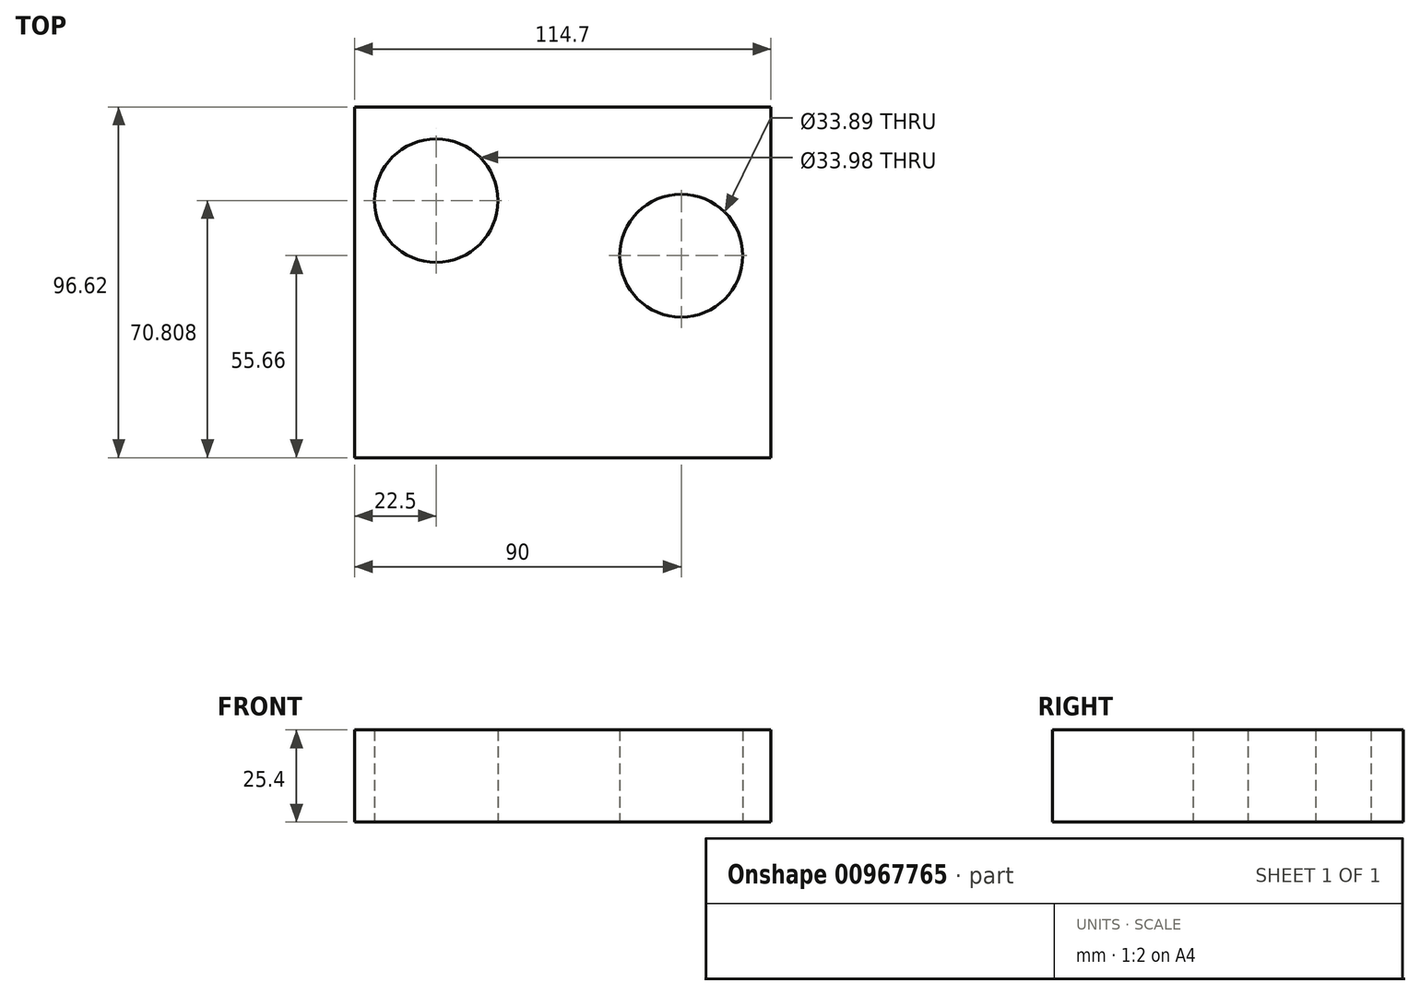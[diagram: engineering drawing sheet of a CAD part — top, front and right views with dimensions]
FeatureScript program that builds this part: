
annotation { "Feature Type Name" : "Feature", "Feature Type Description" : "" }
export const myFeature = defineFeature(function(context is Context, id is Id, definition is map)
    precondition{}
    {
        {
            var Q0;
            Q0=qCreatedBy(makeId("Top.planeOp"),FACE);
            var sketch = newSketch(context, id + "F0", { "sketchPlane" : qUnion([Q0])});
            skLineSegment(sketch, "E0.bottom", {"start": v(-51.86, 40.96) * mm, "end": v(62.84, 40.96) * mm});
            skLineSegment(sketch, "E0.top", {"start": v(-51.86, -55.66) * mm, "end": v(62.84, -55.66) * mm});
            skLineSegment(sketch, "E0.left", {"start": v(-51.86, 40.96) * mm, "end": v(-51.86, -55.66) * mm});
            skLineSegment(sketch, "E0.right", {"start": v(62.84, 40.96) * mm, "end": v(62.84, -55.66) * mm});
            skCircle(sketch, "E1", {"center": v(38.14, 0) * mm, "radius": 16.95 * mm});
            skCircle(sketch, "E2", {"center": v(-29.36, 15.15) * mm, "radius": 17 * mm});
            skSolve(sketch);
        }
        {
            var Q0;
            Q0=makeQuery(id+"F0.imprint","IMPRINT",FACE,{"disambiguationData":[TD([[makeQuery(id+"F0.imprint","IMPRINT",EDGE,{"derivedFrom":sQuery(id+"F0.wireOp",EDGE,"E0.bottom")}),-1.0]])]});
            extrude(context, id + "F1", {"entities" : qUnion([Q0]), "depth" : 25.4 * mm, "offsetDistance" : 25.4 * mm});
        }
    });
